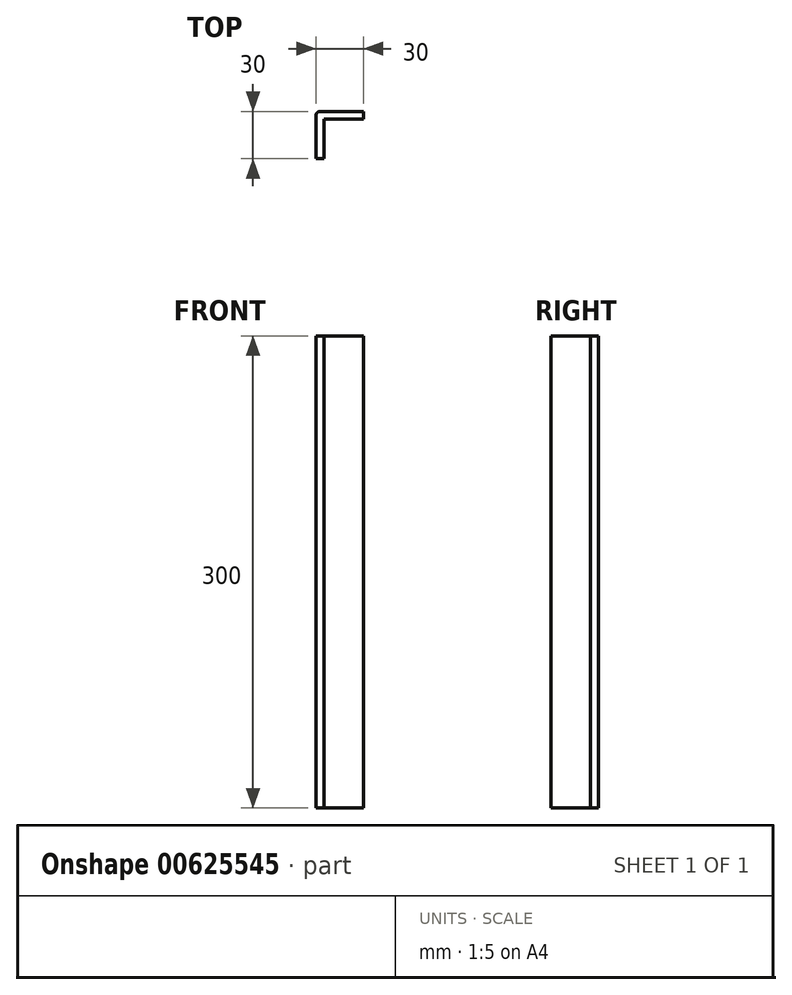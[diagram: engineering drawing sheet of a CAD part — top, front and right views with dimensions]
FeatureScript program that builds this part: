
annotation { "Feature Type Name" : "Feature", "Feature Type Description" : "" }
export const myFeature = defineFeature(function(context is Context, id is Id, definition is map)
    precondition{}
    {
        {
            var Q0;
            Q0=qCreatedBy(makeId("Top.planeOp"),FACE);
            var sketch = newSketch(context, id + "F0", { "sketchPlane" : qUnion([Q0])});
            skLineSegment(sketch, "E0.bottom", {"start": v(-12.5, 15) * mm, "end": v(15, 15) * mm});
            skLineSegment(sketch, "E0.top", {"start": v(-15, -15) * mm, "end": v(-10, -15) * mm});
            skLineSegment(sketch, "E0.left", {"start": v(-15, 12.5) * mm, "end": v(-15, -15) * mm});
            skLineSegment(sketch, "E0.right", {"start": v(15, 15) * mm, "end": v(15, 10) * mm});
            skPoint(sketch, "E0.middle", {"position": v(0, 0) * mm});
            skLineSegment(sketch, "E1", {"start": v(15, 10) * mm, "end": v(-10, 10) * mm});
            skLineSegment(sketch, "E2", {"start": v(-10, 10) * mm, "end": v(-10, -15) * mm});
            skPoint(sketch, "E3.orphan", {"position": v(15, -15) * mm});
            skPoint(sketch, "E4.visualSharp", {"position": v(-15, 15) * mm});
            skArc(sketch, "E4.filletArc", {"start": v(-12.5, 15) * mm, "mid": v(-14.27, 14.27) * mm, "end": v(-15, 12.5) * mm});
            skPoint(sketch, "E5.visualSharp", {"position": v(-10, 10) * mm});
            skLineSegment(sketch, "E5.filletArc", {"start": v(-10, 10) * mm, "end": v(-10, 10) * mm});
            skSolve(sketch);
        }
        {
            var Q0;
            Q0=makeQuery(id+"F0.imprint","IMPRINT",FACE,{"disambiguationData":[TD([[makeQuery(id+"F0.imprint","IMPRINT",EDGE,{"derivedFrom":sQuery(id+"F0.wireOp",EDGE,"E0.bottom")}),-1.0]])]});
            extrude(context, id + "F1", {"entities" : qUnion([Q0]), "depth" : 300 * mm, "offsetDistance" : 25 * mm});
        }
    });
